# Revit family: Wicline_75_Open_in_standard_single_casement
name_source: partatom
category: Windows
revit_build: Autodesk Revit Architecture 2014 (Build: 20130308_1515(x64)
units: mm (PartAtom-declared; Revit-internal decimal feet)

## types (1)
- Wicline_75_Open_in_standard_single_casement
    Acoustic = Rw (C;Ctr) = 47 (-1;-4) dB
    Air Permeability = Class 5
    Bullet resistance = FB4 S, FB4 NS (depending on profile combinations)
    Date of publishing = 3/14/2015
    Default Sill Height = 800 mm
    Description = WICONA’s WICLINE 75 TOP is a window system which is equivalent to passive house standards in energy performance. It combines ease of fabrication and the unrivalled quality of conventional aluminium window systems with a 75 mm frame depth and the highest levels thermal performance from one single system.
    Design country = Germany
    EN1627 Burglar Resistance = RC1N, RC2N, RC2, RC3
    Edition number = 1
    Frame 1017001 = No
    Frame 1017003 = No
    Frame 1017004 = No
    Frame 1017005 = Yes
    Frame 1017006 = No
    Frame Material = WICONA - Aluminium - RAL7016 - Anthracite Grey - Matt
    Frame Thickness = 75 mm  [stored 0.246063 ft]
    Frame Width = 75 mm  [stored 0.246063 ft]
    Frame Width 2 = 50 mm  [stored 0.164042 ft]
    Glass Material = WICONA -  Glass
    Handle Material = Aluminium
    Height = 1500 mm  [stored 4.92126 ft]
    Leaf Height = 1350 mm  [stored 4.42913 ft]
    Leaf Material = WICONA - Aluminium - RAL7016 - Anthracite Grey - Matt
    Leaf Width = 850 mm  [stored 2.78871 ft]
    Load Bearing Capacity of Safety Devices = Passed
    Manufacturer = Wicona
    Manufacturer country = Germany
    Manufacturer name = Wicona
    Material main = Aluminium
    Material secondary = Glass
    Maximum Sash Weight = 150kg as standard design, heavier weights can easily be customised
    Mechanical Strength = Class 4
    Model = Wicline 75 TOP
    Nominal height = 130000
    Nominal width = 100000
    Operating Forces = Class 1
    Operation = IFC_WINDOWCASEMENT
    Product Guid = 634b88b1-3b97-4f89-a69a-c855bc4c2ef3
    Product SKU = WICLINE_75_TOP_W
    Product data url = http://bimobject.com
    Product family = Windows & Doors
    Product group = Windows
    QR code = http://bimobject.com
    Quality Assurance = Certified according to ISO 9001:2008
    Repeated Opening/Closing = Class 3 (20,000 cycles)
    Resistance to wind load = Class C5/B5
    Side Frame 1017101 = No
    Side Frame 1017102 = No
    Side Frame 1017103 = Yes
    Side Frame 1017104 = No
    Side Frame 1017115 = No
    URL = http://www.wicona.com
    Wall Closure = By host
    Watertightness = E900
    Weight Net (Kg) = 0
    Width = 1000 mm  [stored 3.28084 ft]
    Window Offset = 60 mm  [stored 0.19685 ft]

note: [stored X ft] marks values corroborated as IEEE doubles in the binary element streams (Revit-internal decimal feet)

## geometry (parser evidence)
native form markers: Blend x4, Sweep x9
no freeform markers — native parametric forms only
